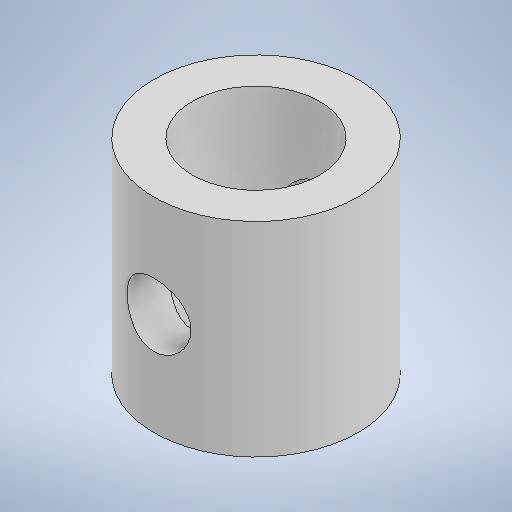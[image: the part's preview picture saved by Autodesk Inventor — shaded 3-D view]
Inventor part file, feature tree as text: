
AUTODESK INVENTOR PART (.ipt)
format: ipt  version: 2025.1 (Build 291241000, 241)  size: 220,672 bytes
history: native  units: mm
features: sketch x2, extrude x1, plane x1, hole x1
ambient origin geometry x8: Origin, YZ Plane, XZ Plane, XY Plane, X Axis, Y Axis, Z Axis, Center Point
bodies: Solid1 (feature_tree)
feature tree (5):
  extrude  "Extrusion1"  Depth=5.0mm
  plane  "Work Plane1"
  hole  "Hole1"  [1 undecoded]
  sketch  "Sketch1"  dims[d0=8.0mm d1=5.0mm]
  sketch  "Sketch2"  dims[d2=8.0mm d3=0.0mm d4=4.0mm d5=2.5mm d6=6.0mm d7=4.0mm d8=2.0mm d9=90.0deg d10=8.0mm d11=0.0mm]
note: 1 required parameter value undecoded (feature->parameter linkage not recoverable at this tier; creation-order binding heuristic only, values carry confidence <= 0.55)
